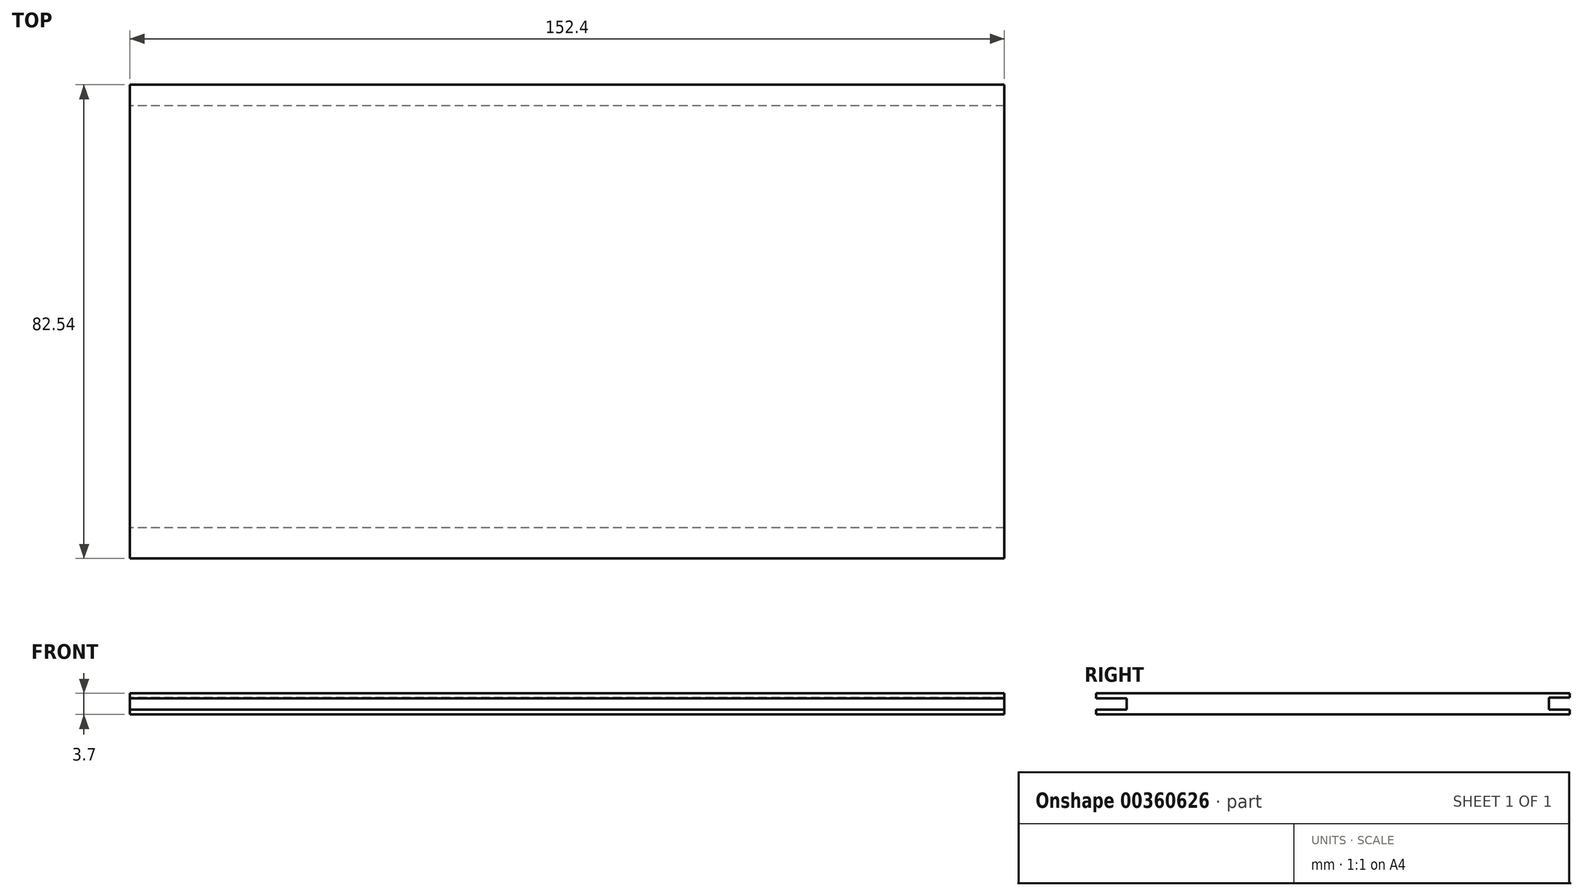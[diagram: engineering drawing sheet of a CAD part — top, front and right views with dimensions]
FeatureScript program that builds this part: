
annotation { "Feature Type Name" : "Feature", "Feature Type Description" : "" }
export const myFeature = defineFeature(function(context is Context, id is Id, definition is map)
    precondition{}
    {
        {
            var Q0;
            Q0=qCreatedBy(makeId("Top.planeOp"),FACE);
            var sketch = newSketch(context, id + "F0", { "sketchPlane" : qUnion([Q0])});
            skLineSegment(sketch, "E0.bottom", {"start": v(-76.2, 41.28) * mm, "end": v(76.2, 41.28) * mm});
            skLineSegment(sketch, "E0.top", {"start": v(-76.2, -41.28) * mm, "end": v(76.2, -41.28) * mm});
            skLineSegment(sketch, "E0.left", {"start": v(-76.2, 41.28) * mm, "end": v(-76.2, -41.28) * mm});
            skLineSegment(sketch, "E0.right", {"start": v(76.2, 41.28) * mm, "end": v(76.2, -41.28) * mm});
            skPoint(sketch, "E0.middle", {"position": v(0, 0) * mm});
            skSolve(sketch);
        }
        {
            var Q0;
            Q0=makeQuery(id+"F0.imprint","IMPRINT",FACE,{"disambiguationData":[TD([[makeQuery(id+"F0.imprint","IMPRINT",EDGE,{"derivedFrom":sQuery(id+"F0.wireOp",EDGE,"E0.bottom")}),-1.0]])]});
            extrude(context, id + "F1", {"entities" : qUnion([Q0]), "depth" : 3.7 * mm});
        }
        {
            var Q0;
            Q0=makeQuery(id+"F1.opExtrude","SWEPT_FACE",FACE,{"disambiguationData":[OSD([sQuery(id+"F0.wireOp",EDGE,"E0.left")])]});
            var sketch = newSketch(context, id + "F2", { "sketchPlane" : qUnion([Q0])});
            skLineSegment(sketch, "E1.bottom", {"start": v(-41.27, 2.91) * mm, "end": v(-37.63, 2.91) * mm});
            skLineSegment(sketch, "E1.top", {"start": v(-41.27, 0.83) * mm, "end": v(-37.63, 0.83) * mm});
            skLineSegment(sketch, "E1.left", {"start": v(-41.27, 2.91) * mm, "end": v(-41.27, 0.83) * mm});
            skLineSegment(sketch, "E1.right", {"start": v(-37.63, 2.91) * mm, "end": v(-37.63, 0.83) * mm});
            skLineSegment(sketch, "E2.bottom", {"start": v(41.28, 2.8) * mm, "end": v(35.93, 2.8) * mm});
            skLineSegment(sketch, "E2.top", {"start": v(41.28, 0.83) * mm, "end": v(35.93, 0.83) * mm});
            skLineSegment(sketch, "E2.left", {"start": v(41.28, 2.8) * mm, "end": v(41.28, 0.83) * mm});
            skLineSegment(sketch, "E2.right", {"start": v(35.93, 2.8) * mm, "end": v(35.93, 0.83) * mm});
            skSolve(sketch);
        }
        {
            var Q0;
            Q0 = qSketchRegion(id + "F2", true);
            extrude(context, id + "F3", {"entities" : qUnion([Q0]), "operationType" : NewBodyOperationType.REMOVE, "oppositeDirection" : true, "depth" : 167.39 * mm});
        }
    });
